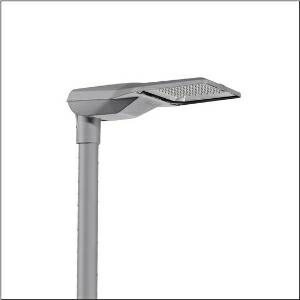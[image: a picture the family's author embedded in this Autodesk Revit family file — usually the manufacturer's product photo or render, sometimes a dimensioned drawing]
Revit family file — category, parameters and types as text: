
# Revit family: streetlight_sl_21_iq_midi___st0_5a_5xe3b31g08nb_5b56
name_source: partatom
category: Lighting Fixtures
units: mm (PartAtom-declared; Revit-internal decimal feet)

## family parameters
Cut with Voids When Loaded = No
Host = Face
Light Source = No
Part Type = Normal
Room Calculation Point = No
Round Connector Dimension = Use Diameter
Shared = No

## types (1)
- --- (1 x LED, 23230 lm, 155.5 W, 3000K)
    Apparent Load = 155 VA
    CIE Flux Codes = 43 76 97 100 100
    Color Rendering = 70
    Color Temperature = 3000K
    Default Elevation = 1800 mm
    Description = Streetlight SL 21 iQ midi, mast luminaire, primary light control with lens, of PMMA, primary optical cover: cover, of toughened safety glass, transparent, light distribution: ST0.5a, light emission: direct distribution, primary light characteristic: asymmetric, installation type: post-top, side-entry, LED, High Power LED, rated luminous flux: 23.230lm, luminous efficacy: 149lm/W, light colour: 730, colour temperature: 3000K, control gear: iQ Street-Remote, control: Street-Remote, Auto-Match, Temp-Guard, Lumen-Switch, Night-Set, Smart-Wire, Light-Fading, Desk-Remote (wireless, voltage-free reading and setting of iQ features in the workshop via application-optimized NFC function/RFID function), optimised constant luminous flux control (CLO 2.0), pre-setting: linear dimming characteristic, mains connection: 230..240V, AC, 50/60Hz, start of lifetime: 156W, end of service life: 162W, reduction: 69W, luminaire housing, of diecast aluminium, powder-coated, Siteco® metallic grey (DB 702S), corrosivity category C5 mid according to DIN EN ISO 12944, please order mast flange separately, inclination adjustable: 0°, 5°, 10°, 15°, sealing non-destructively replaceable, multi-level sealing system, length: 644mm, width: 335mm, height: 110mm, mast flange for spigot size: 42mm (side-entry): 5XC10008XM4, 60/48mm (side-entry/post-top): 5XC10108XM2, 76/60mm (side-entry/post-top): 5XC10108XM1, mounting height: 4..8m, protection rating (complete): IP66, insulation class (complete): insulation class II (safety insulation), certification: CE, ENEC, ENEC+, VDE, impact resistance: IK10, permissible operating ambient temperature for outdoor applications: -40..+50°C, standard-compliant lighting for roads and squares, packaging unit: 1 piece

Light Distribution: ST0.5a
    Height = 111 mm
    Lamp = 1 x LED
    Lamp Light Flux = 23230 lm
    Lamp Power = 155.5 W
    Lamp count = 1
    Length = 644 mm
    Luminous efficacy = 149 lm/W
    Manufacturer = Siteco
    ModVariant = No
    Model = 5XE3B31G08NB
    Number of Poles = 1
    OnlyDefault = Yes
    Power Factor = 1
    Product Name = Streetlight SL 21 iQ midi | ST0.5a
    Product group = mast luminaire | pylon top
    ProductGroupID = 6100
    Protection Class = Protection class II
    Protection Degree = IP 66
    RLX_Detail_Level = 1
    RLX_Emergency_Light_Flux = 0 lm
    RLX_Emergency_Type = 0
    RLX_Emergency_Type_DB = No
    RlxData = <blob elided: 38349 chars, md5=fee46164>
    Socket = socket
    Standby Power = 0 W
    System Light Flux = 23230 lm
    System Power = 155 W
    Type Comments = factory setting: luminous flux: 100 % | dim-lin: 254 | 823 mA
    Type Image = l_1004298.jpg
    URL = http://relux.com
    VarID = @adj_171546
    Voltage = 0 V
    Weight = 0.00 kg
    Width = 336 mm

## geometry (parser evidence)
native form markers: Blend x4, Sweep x9
no freeform markers — native parametric forms only
